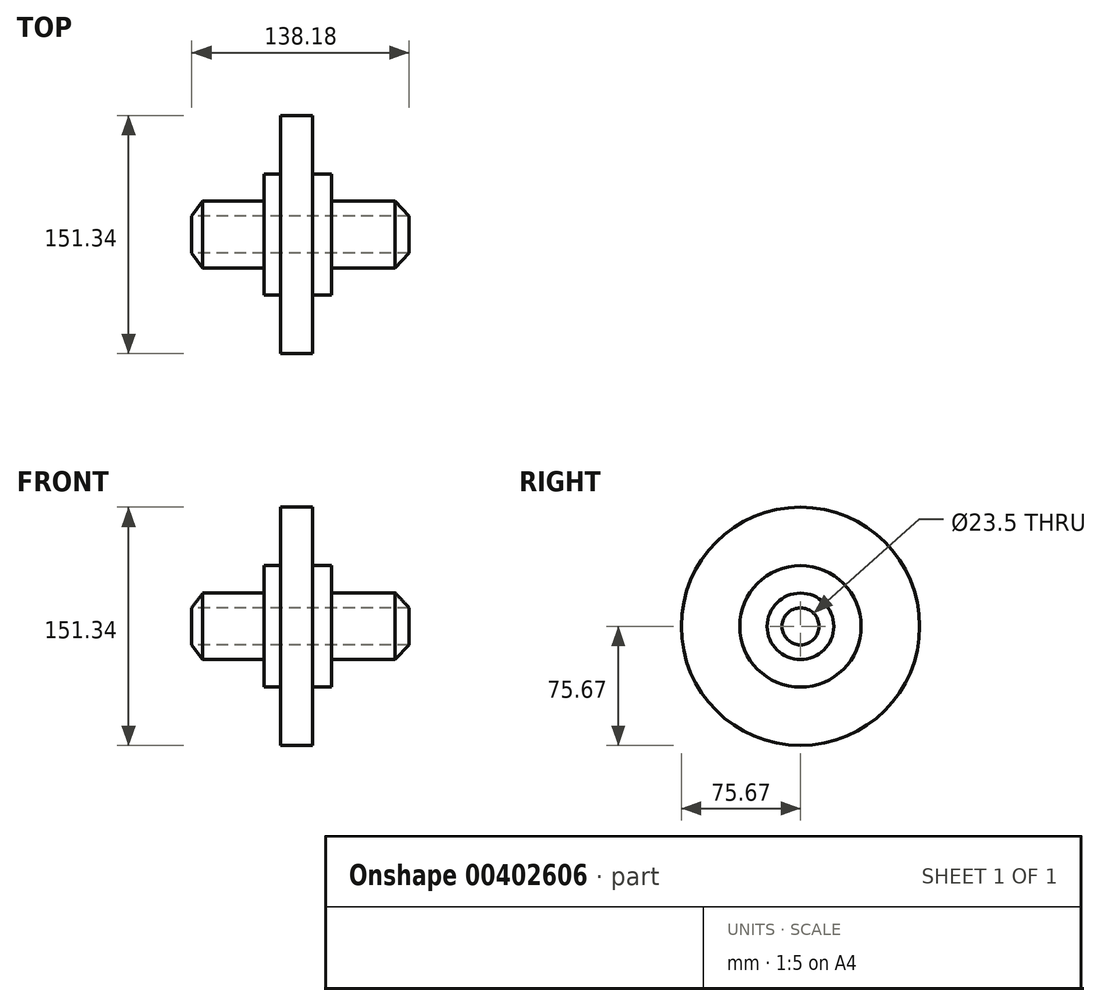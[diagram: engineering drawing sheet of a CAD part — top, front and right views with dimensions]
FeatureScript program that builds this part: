
annotation { "Feature Type Name" : "Feature", "Feature Type Description" : "" }
export const myFeature = defineFeature(function(context is Context, id is Id, definition is map)
    precondition{}
    {
        {
            var Q0;
            Q0=qCreatedBy(makeId("Front.planeOp"),FACE);
            var sketch = newSketch(context, id + "F0", { "sketchPlane" : qUnion([Q0])});
            skLineSegment(sketch, "E0", {"start": v(-66.74, 0) * mm, "end": v(-59.69, 9.4) * mm});
            skLineSegment(sketch, "E1", {"start": v(-59.69, 9.4) * mm, "end": v(-20.68, 9.4) * mm});
            skLineSegment(sketch, "E2", {"start": v(-20.68, 9.4) * mm, "end": v(-20.68, 26.79) * mm});
            skLineSegment(sketch, "E3", {"start": v(-20.68, 26.79) * mm, "end": v(-10.34, 26.79) * mm});
            skLineSegment(sketch, "E4", {"start": v(-10.34, 26.79) * mm, "end": v(-10.34, 63.92) * mm});
            skLineSegment(sketch, "E5", {"start": v(-10.34, 63.92) * mm, "end": v(9.87, 63.92) * mm});
            skLineSegment(sketch, "E6", {"start": v(9.87, 63.92) * mm, "end": v(9.87, 26.79) * mm});
            skLineSegment(sketch, "E7", {"start": v(9.87, 26.79) * mm, "end": v(22.09, 26.79) * mm});
            skLineSegment(sketch, "E8", {"start": v(22.09, 26.79) * mm, "end": v(22.09, 9.4) * mm});
            skLineSegment(sketch, "E9", {"start": v(22.09, 9.4) * mm, "end": v(62.5, 9.4) * mm});
            skLineSegment(sketch, "E10", {"start": v(62.5, 9.4) * mm, "end": v(71.44, 0) * mm});
            skLineSegment(sketch, "E11", {"start": v(71.44, 0) * mm, "end": v(-66.74, 0) * mm});
            skLineSegment(sketch, "E12", {"start": v(-102.93, -11.75) * mm, "end": v(89.3, -11.75) * mm});
            skSolve(sketch);
        }
        {
            var Q0;
            Q0=makeQuery(id+"F0.imprint","IMPRINT",FACE,{"disambiguationData":[TD([[makeQuery(id+"F0.imprint","IMPRINT",EDGE,{"derivedFrom":sQuery(id+"F0.wireOp",EDGE,"E0")}),-1.0]])]});
            var Q1;
            Q1=sQuery(id+"F0.wireOp",EDGE,"E12");
            revolve(context, id + "F1", {"entities" : qUnion([Q0]), "axis" : qUnion([Q1]), "revolveType" : RevolveType.FULL});
        }
    });
